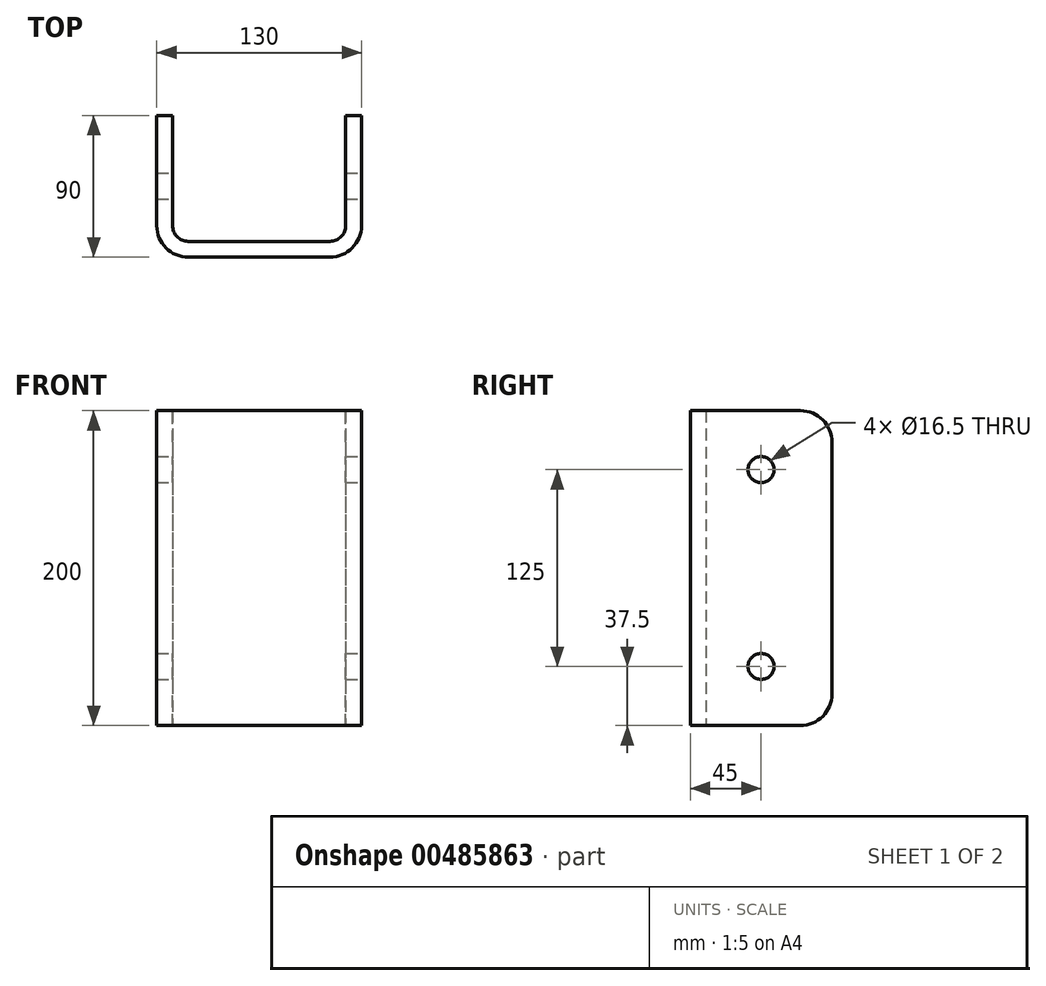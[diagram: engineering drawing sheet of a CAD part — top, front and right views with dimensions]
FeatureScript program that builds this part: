
annotation { "Feature Type Name" : "Feature", "Feature Type Description" : "" }
export const myFeature = defineFeature(function(context is Context, id is Id, definition is map)
    precondition{}
    {
        {
            var Q0;
            Q0=qCreatedBy(makeId("Top.planeOp"),FACE);
            var sketch = newSketch(context, id + "F0", { "sketchPlane" : qUnion([Q0])});
            skLineSegment(sketch, "E0.top", {"start": v(45, -45) * mm, "end": v(-45, -45) * mm});
            skLineSegment(sketch, "E0.left", {"start": v(65, 45) * mm, "end": v(65, -25) * mm});
            skLineSegment(sketch, "E0.right", {"start": v(-65, 45) * mm, "end": v(-65, -25) * mm});
            skPoint(sketch, "E0.middle", {"position": v(0, 0) * mm});
            skPoint(sketch, "E1.visualSharp", {"position": v(-65, -45) * mm});
            skArc(sketch, "E1.filletArc", {"start": v(-65, -25) * mm, "mid": v(-59.14, -39.14) * mm, "end": v(-45, -45) * mm});
            skPoint(sketch, "E2.visualSharp", {"position": v(65, -45) * mm});
            skArc(sketch, "E2.filletArc", {"start": v(45, -45) * mm, "mid": v(59.14, -39.14) * mm, "end": v(65, -25) * mm});
            skLineSegment(sketch, "E3.0", {"start": v(55, 45) * mm, "end": v(55, -25) * mm});
            skLineSegment(sketch, "E3.1", {"start": v(-55, 45) * mm, "end": v(-55, -25) * mm});
            skArc(sketch, "E3.2", {"start": v(-55, -25) * mm, "mid": v(-52.07, -32.07) * mm, "end": v(-45, -35) * mm});
            skLineSegment(sketch, "E3.3", {"start": v(45, -35) * mm, "end": v(-45, -35) * mm});
            skArc(sketch, "E3.4", {"start": v(45, -35) * mm, "mid": v(52.07, -32.07) * mm, "end": v(55, -25) * mm});
            skLineSegment(sketch, "E4", {"start": v(-55, 45) * mm, "end": v(-65, 45) * mm});
            skLineSegment(sketch, "E5", {"start": v(55, 45) * mm, "end": v(65, 45) * mm});
            skSolve(sketch);
        }
        {
            var Q0;
            Q0 = qSketchRegion(id + "F0", true);
            extrude(context, id + "F1", {"entities" : qUnion([Q0]), "endBound" : BoundingType.SYMMETRIC, "depth" : 200 * mm});
        }
        {
            var Q0;
            Q0=makeQuery(id+"F1.opExtrude","SWEPT_FACE",FACE,{"disambiguationData":[OSD([sQuery(id+"F0.wireOp",EDGE,"E0.left")])]});
            var sketch = newSketch(context, id + "F2", { "sketchPlane" : qUnion([Q0])});
            skLineSegment(sketch, "E6", {"start": v(0, 100) * mm, "end": v(0, -100) * mm, "construction": true});
            skCircle(sketch, "E7", {"center": v(0, 62.5) * mm, "radius": 8.25 * mm});
            skCircle(sketch, "E8", {"center": v(0, -62.5) * mm, "radius": 8.25 * mm});
            skSolve(sketch);
        }
        {
            var Q0;
            Q0 = qSketchRegion(id + "F2", true);
            extrude(context, id + "F3", {"entities" : qUnion([Q0]), "operationType" : NewBodyOperationType.REMOVE, "endBound" : BoundingType.THROUGH_ALL, "oppositeDirection" : true, "depth" : 25 * mm});
        }
        {
            var Q0;
            Q0=makeQuery(id+"F1.opExtrude","CAP_EDGE",EDGE,{"disambiguationData":[OSD([sQuery(id+"F0.wireOp",EDGE,"E5")])],"isStart":false});
            var Q1;
            Q1=makeQuery(id+"F1.opExtrude","CAP_EDGE",EDGE,{"disambiguationData":[OSD([sQuery(id+"F0.wireOp",EDGE,"E4")])],"isStart":false});
            var Q2;
            Q2=makeQuery(id+"F1.opExtrude","CAP_EDGE",EDGE,{"disambiguationData":[OSD([sQuery(id+"F0.wireOp",EDGE,"E4")])],"isStart":true});
            var Q3;
            Q3=makeQuery(id+"F1.opExtrude","CAP_EDGE",EDGE,{"disambiguationData":[OSD([sQuery(id+"F0.wireOp",EDGE,"E5")])],"isStart":true});
            fillet(context, id + "F4", {"entities" : qUnion([Q0, Q1, Q2, Q3]), "radius" : 20 * mm, "tangentPropagation" : true, "allowEdgeOverflow" : false});
        }
    });
